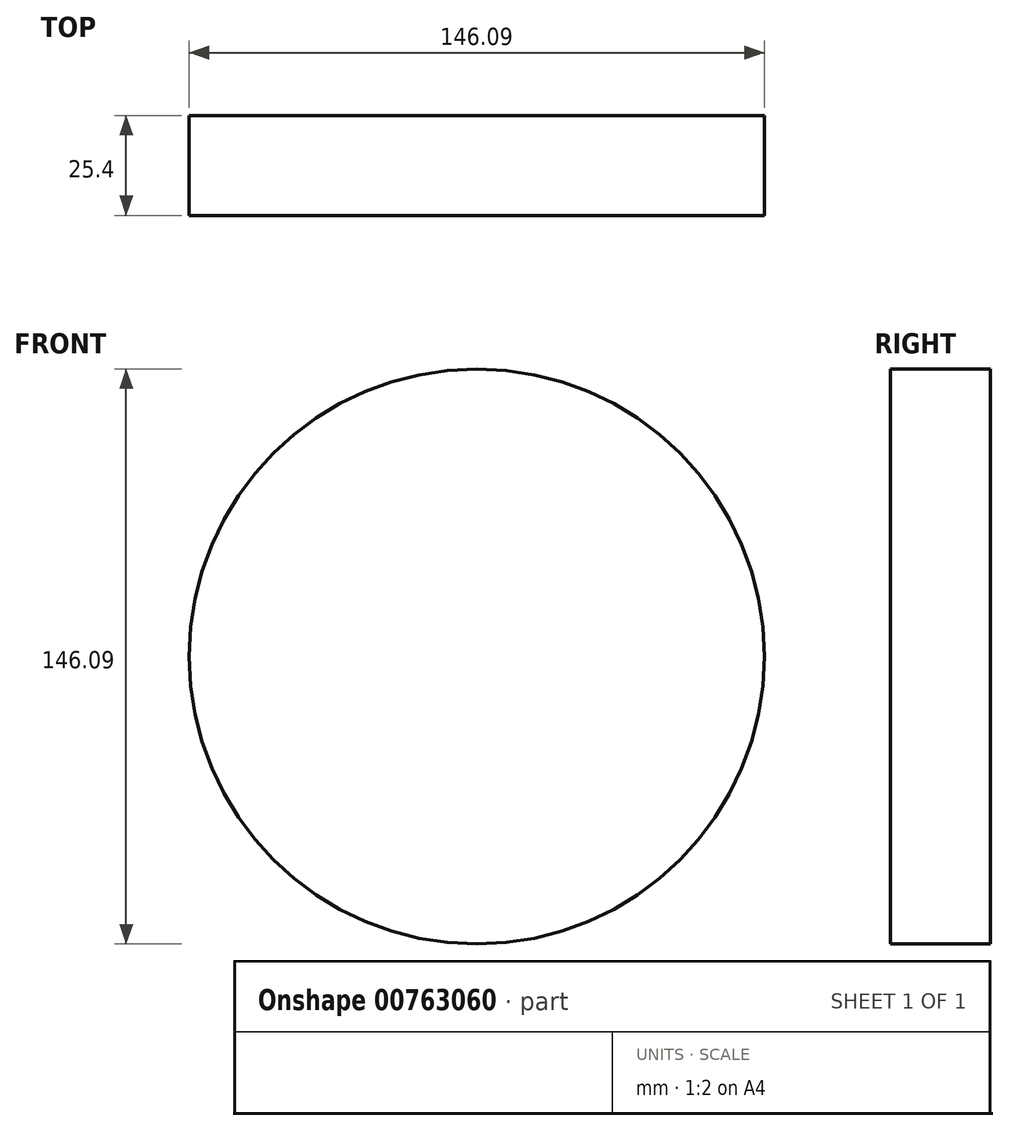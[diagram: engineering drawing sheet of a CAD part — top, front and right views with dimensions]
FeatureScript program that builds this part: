
annotation { "Feature Type Name" : "Feature", "Feature Type Description" : "" }
export const myFeature = defineFeature(function(context is Context, id is Id, definition is map)
    precondition{}
    {
        {
            var Q0;
            Q0=qCreatedBy(makeId("Front.planeOp"),FACE);
            var sketch = newSketch(context, id + "F0", { "sketchPlane" : qUnion([Q0])});
            skLineSegment(sketch, "E0.bottom", {"start": v(-93.3, 59.67) * mm, "end": v(-92.94, 59.67) * mm});
            skLineSegment(sketch, "E0.top", {"start": v(-93.3, 47.1) * mm, "end": v(-92.94, 47.1) * mm});
            skLineSegment(sketch, "E0.left", {"start": v(-93.3, 59.67) * mm, "end": v(-93.3, 47.1) * mm});
            skLineSegment(sketch, "E0.right", {"start": v(-92.94, 59.67) * mm, "end": v(-92.94, 47.1) * mm});
            skCircle(sketch, "E1", {"center": v(44, 46.85) * mm, "radius": 73.05 * mm});
            skSolve(sketch);
        }
        {
            var Q0;
            Q0=makeQuery(id+"F0.imprint","IMPRINT",FACE,{"disambiguationData":[TD([[makeQuery(id+"F0.imprint","IMPRINT",EDGE,{"derivedFrom":sQuery(id+"F0.wireOp",EDGE,"E1")}),1.0]])]});
            extrude(context, id + "F1", {"entities" : qUnion([Q0]), "depth" : 25.4 * mm, "offsetDistance" : 25.4 * mm});
        }
    });
